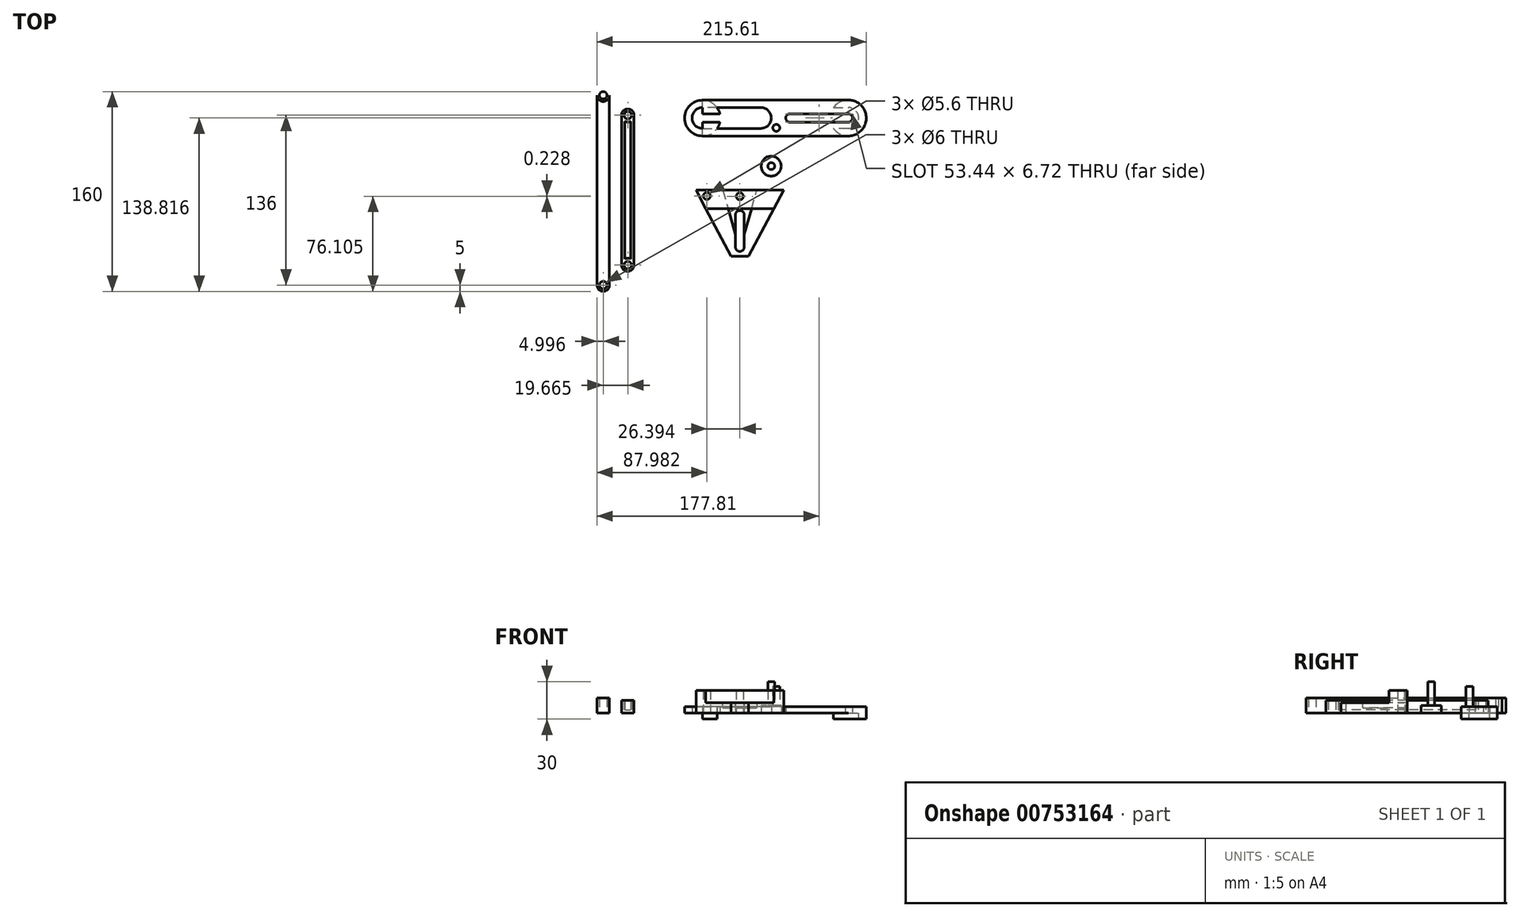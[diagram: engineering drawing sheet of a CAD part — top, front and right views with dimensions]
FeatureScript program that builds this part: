
annotation { "Feature Type Name" : "Feature", "Feature Type Description" : "" }
export const myFeature = defineFeature(function(context is Context, id is Id, definition is map)
    precondition{}
    {
        {
            var Q0;
            Q0=qCreatedBy(makeId("Top.planeOp"),FACE);
            var sketch = newSketch(context, id + "F0", { "sketchPlane" : qUnion([Q0])});
            skLineSegment(sketch, "E0.bottom", {"start": v(-59.67, 60) * mm, "end": v(-49.67, 60) * mm});
            skLineSegment(sketch, "E0.top", {"start": v(-59.67, 0) * mm, "end": v(-49.67, 0) * mm});
            skLineSegment(sketch, "E0.left", {"start": v(-59.67, 60) * mm, "end": v(-59.67, 0) * mm});
            skLineSegment(sketch, "E0.right", {"start": v(-49.67, 60) * mm, "end": v(-49.67, 0) * mm});
            skCircle(sketch, "E1", {"center": v(-54.67, 60) * mm, "radius": 5 * mm});
            skCircle(sketch, "E2.0", {"center": v(-54.67, 60) * mm, "radius": 3 * mm});
            skLineSegment(sketch, "E3.MirrorCS", {"start": v(-59.67, -60) * mm, "end": v(-49.67, -60) * mm});
            skLineSegment(sketch, "E4.MirrorCS", {"start": v(-49.67, -60) * mm, "end": v(-49.67, 0) * mm});
            skLineSegment(sketch, "E5.MirrorCS", {"start": v(-59.67, -60) * mm, "end": v(-59.67, 0) * mm});
            skCircle(sketch, "E6.MirrorC", {"center": v(-54.67, -60) * mm, "radius": 3 * mm});
            skCircle(sketch, "E7.MirrorC", {"center": v(-54.67, -60) * mm, "radius": 5 * mm});
            skSolve(sketch);
        }
        {
            var Q0;
            Q0 = qSketchRegion(id + "F0", true);
            extrude(context, id + "F1", {"entities" : qUnion([Q0]), "depth" : 10 * mm, "offsetDistance" : 25 * mm});
        }
        {
            var Q0;
            Q0=makeQuery(id+"F1.opExtrude","CAP_FACE",FACE,{"disambiguationData":[OSD([sQuery(id+"F0.wireOp",EDGE,"E0.left"),sQuery(id+"F0.wireOp",EDGE,"E0.right"),sQuery(id+"F0.wireOp",EDGE,"E1"),sQuery(id+"F0.wireOp",EDGE,"E2.0"),sQuery(id+"F0.wireOp",EDGE,"E4.MirrorCS"),sQuery(id+"F0.wireOp",EDGE,"E5.MirrorCS"),sQuery(id+"F0.wireOp",EDGE,"E6.MirrorC"),sQuery(id+"F0.wireOp",EDGE,"E7.MirrorC")])],"isStart":false});
            shell(context, id + "F2", {"entities" : qUnion([Q0]), "thickness" : 2.5 * mm});
        }
        {
            var Q0;
            Q0=qCreatedBy(makeId("Top.planeOp"),FACE);
            var sketch = newSketch(context, id + "F3", { "sketchPlane" : qUnion([Q0])});
            skLineSegment(sketch, "E8", {"start": v(70.1, 0) * mm, "end": v(42.05, -53.04) * mm});
            skLineSegment(sketch, "E9", {"start": v(42.05, -53.04) * mm, "end": v(28.05, -53.04) * mm});
            skLineSegment(sketch, "E10", {"start": v(28.05, -53.04) * mm, "end": v(0, 0) * mm});
            skLineSegment(sketch, "E11", {"start": v(0, 0) * mm, "end": v(70.1, 0) * mm});
            skCircle(sketch, "E12", {"center": v(61.44, -4.67) * mm, "radius": 2.8 * mm});
            skCircle(sketch, "E13", {"center": v(35.05, -4.9) * mm, "radius": 2.8 * mm});
            skPoint(sketch, "E13.centerSnap0", {"position": v(35.05, -53.04) * mm});
            skLineSegment(sketch, "E14", {"start": v(35.05, -53.04) * mm, "end": v(35.05, 0) * mm, "construction": true});
            skCircle(sketch, "E15.MirrorC", {"center": v(8.65, -4.67) * mm, "radius": 2.8 * mm});
            skLineSegment(sketch, "E16", {"start": v(62.33, -14.67) * mm, "end": v(7.76, -14.67) * mm});
            skCircle(sketch, "E17", {"center": v(35.05, -45.57) * mm, "radius": 3.5 * mm});
            skCircle(sketch, "E18", {"center": v(35.05, -19.75) * mm, "radius": 3.5 * mm});
            skLineSegment(sketch, "E19", {"start": v(38.55, -45.57) * mm, "end": v(38.55, -19.75) * mm});
            skLineSegment(sketch, "E20", {"start": v(31.55, -45.57) * mm, "end": v(31.55, -19.75) * mm});
            skSolve(sketch);
        }
        {
            var Q0;
            Q0 = qSketchRegion(id + "F3", true);
            extrude(context, id + "F4", {"entities" : qUnion([Q0]), "depth" : 8 * mm, "offsetDistance" : 25 * mm});
        }
        {
            var Q0;
            {var subQ2=sQuery(id+"F3.wireOp",EDGE,"E9");Q0=makeQuery(id+"F3.imprint","IMPRINT",FACE,{"disambiguationData":[TD([[makeQuery(id+"F3.imprint","IMPRINT",EDGE,{"derivedFrom":subQ2}),-1.0]])]});}
            var Q1;
            {var subQ0=sQuery(id+"F3.wireOp",EDGE,"E11");Q1=makeQuery(id+"F3.imprint","IMPRINT",FACE,{"disambiguationData":[TD([[makeQuery(id+"F3.imprint","IMPRINT",EDGE,{"derivedFrom":subQ0}),-1.0]])]});}
            extrude(context, id + "F5", {"entities" : qUnion([Q0, Q1]), "depth" : 8 * mm, "offsetDistance" : 25 * mm});
        }
        {
            var Q0;
            Q0=makeQuery(id+"F4.opExtrude","CAP_FACE",FACE,{"disambiguationData":[OSD([sQuery(id+"F3.wireOp",EDGE,"E8"),sQuery(id+"F3.wireOp",EDGE,"E9"),sQuery(id+"F3.wireOp",EDGE,"E10"),sQuery(id+"F3.wireOp",EDGE,"E16")])],"isStart":false});
            shell(context, id + "F6", {"entities" : qUnion([Q0]), "thickness" : 2.5 * mm});
        }
        {
            var Q0;
            Q0=makeQuery(id+"F3.imprint","IMPRINT",FACE,{"disambiguationData":[TD([[makeQuery(id+"F3.imprint","IMPRINT",EDGE,{"derivedFrom":sQuery(id+"F3.wireOp",EDGE,"E12")}),1.0]])]});
            var Q1;
            Q1=makeQuery(id+"F3.imprint","IMPRINT",FACE,{"disambiguationData":[TD([[makeQuery(id+"F3.imprint","IMPRINT",EDGE,{"derivedFrom":sQuery(id+"F3.wireOp",EDGE,"E15.MirrorC")}),-1.0]])]});
            extrude(context, id + "F7", {"entities" : qUnion([Q0, Q1]), "operationType" : NewBodyOperationType.ADD, "depth" : 18 * mm, "offsetDistance" : 25 * mm});
        }
        {
            var Q0;
            Q0=qCreatedBy(makeId("Top.planeOp"),FACE);
            var sketch = newSketch(context, id + "F8", { "sketchPlane" : qUnion([Q0])});
            skLineSegment(sketch, "E21.bottom", {"start": v(121.84, 43.38) * mm, "end": v(5.16, 43.38) * mm});
            skLineSegment(sketch, "E21.top", {"start": v(121.84, 72.06) * mm, "end": v(5.16, 72.06) * mm});
            skLineSegment(sketch, "E21.left", {"start": v(121.84, 43.38) * mm, "end": v(121.84, 54.45) * mm});
            skLineSegment(sketch, "E21.right", {"start": v(5.16, 43.38) * mm, "end": v(5.16, 72.06) * mm});
            skCircle(sketch, "E22", {"center": v(121.84, 57.82) * mm, "radius": 14.44 * mm});
            skCircle(sketch, "E23", {"center": v(5.16, 57.72) * mm, "radius": 14.34 * mm});
            skArc(sketch, "E24", {"start": v(121.84, 54.45) * mm, "mid": v(125.2, 57.82) * mm, "end": v(121.84, 61.18) * mm});
            skLineSegment(sketch, "E25", {"start": v(63.5, 43.38) * mm, "end": v(63.5, 72.06) * mm, "construction": true});
            skArc(sketch, "E26", {"start": v(75.12, 61.18) * mm, "mid": v(71.76, 57.82) * mm, "end": v(75.12, 54.45) * mm});
            skLineSegment(sketch, "E27", {"start": v(121.84, 54.45) * mm, "end": v(75.12, 54.45) * mm});
            skLineSegment(sketch, "E28", {"start": v(75.12, 61.18) * mm, "end": v(121.84, 61.18) * mm});
            skCircle(sketch, "E29.MirrorC", {"center": v(51.88, 57.82) * mm, "radius": 3.36 * mm});
            skLineSegment(sketch, "E30.MirrorCS", {"start": v(5.16, 54.45) * mm, "end": v(51.88, 54.45) * mm});
            skLineSegment(sketch, "E31.MirrorCS", {"start": v(51.88, 61.18) * mm, "end": v(5.16, 61.18) * mm});
            skCircle(sketch, "E32.MirrorC", {"center": v(5.16, 57.82) * mm, "radius": 3.36 * mm});
            skLineSegment(sketch, "E33.trimOffspring", {"start": v(121.84, 61.18) * mm, "end": v(121.84, 72.06) * mm});
            skLineSegment(sketch, "E34.0", {"start": v(75.12, 66.18) * mm, "end": v(121.84, 66.18) * mm});
            skArc(sketch, "E34.1", {"start": v(75.12, 66.18) * mm, "mid": v(66.76, 57.82) * mm, "end": v(75.12, 49.45) * mm});
            skLineSegment(sketch, "E34.2", {"start": v(121.84, 49.45) * mm, "end": v(75.12, 49.45) * mm});
            skArc(sketch, "E34.3", {"start": v(121.84, 49.45) * mm, "mid": v(130.2, 57.82) * mm, "end": v(121.84, 66.18) * mm});
            skArc(sketch, "E35.MirrorCS", {"start": v(51.88, 66.18) * mm, "mid": v(60.24, 57.82) * mm, "end": v(51.88, 49.45) * mm});
            skLineSegment(sketch, "E36.MirrorCS", {"start": v(51.88, 66.18) * mm, "end": v(5.16, 66.18) * mm});
            skLineSegment(sketch, "E37.MirrorCS", {"start": v(5.16, 49.45) * mm, "end": v(51.88, 49.45) * mm});
            skArc(sketch, "E38.MirrorCS", {"start": v(5.16, 49.45) * mm, "mid": v(-3.2, 57.82) * mm, "end": v(5.16, 66.18) * mm});
            skSolve(sketch);
        }
        {
            var Q0;
            Q0 = qSketchRegion(id + "F8", true);
            var Q1;
            {var subQ0=sQuery(id+"F8.wireOp",EDGE,"E34.0");var subQ1=sQuery(id+"F8.wireOp",EDGE,"E22");var subQ2=makeQuery(id+"F8.imprint","INTERSECT",VERTEX,{"derivedFrom":[subQ1,subQ0]});Q1=makeQuery(id+"F8.imprint","IMPRINT",FACE,{"disambiguationData":[TD([[makeQuery(id+"F8.imprint","IMPRINT",EDGE,{"disambiguationData":[TD([[subQ2,-1.0]])],"derivedFrom":subQ1}),1.0]])]});}
            var Q2;
            {var subQ0=sQuery(id+"F8.wireOp",EDGE,"E24");Q2=makeQuery(id+"F8.imprint","IMPRINT",FACE,{"disambiguationData":[TD([[makeQuery(id+"F8.imprint","IMPRINT",EDGE,{"derivedFrom":subQ0}),-1.0]])]});}
            var Q3;
            {var subQ1=sQuery(id+"F8.wireOp",EDGE,"E26");Q3=makeQuery(id+"F8.imprint","IMPRINT",FACE,{"disambiguationData":[TD([[makeQuery(id+"F8.imprint","IMPRINT",EDGE,{"derivedFrom":subQ1}),-1.0]])]});}
            var Q4;
            {var subQ0=sQuery(id+"F8.wireOp",EDGE,"E27");var subQ5=sQuery(id+"F8.wireOp",EDGE,"E22");var subQ6=makeQuery(id+"F8.imprint","INTERSECT",VERTEX,{"derivedFrom":[subQ5,subQ0]});Q4=makeQuery(id+"F8.imprint","IMPRINT",FACE,{"disambiguationData":[TD([[makeQuery(id+"F8.imprint","IMPRINT",EDGE,{"disambiguationData":[TD([[subQ6,-1.0]])],"derivedFrom":subQ5}),1.0]])]});}
            var Q5;
            {var subQ12=sQuery(id+"F8.wireOp",EDGE,"E35.MirrorCS");Q5=makeQuery(id+"F8.imprint","IMPRINT",FACE,{"disambiguationData":[TD([[makeQuery(id+"F8.imprint","IMPRINT",EDGE,{"derivedFrom":subQ12}),-1.0]])]});}
            var Q6;
            {var subQ3=sQuery(id+"F8.wireOp",EDGE,"E37.MirrorCS");var subQ5=sQuery(id+"F8.wireOp",EDGE,"E23");var subQ6=makeQuery(id+"F8.imprint","INTERSECT",VERTEX,{"derivedFrom":[subQ5,subQ3]});Q6=makeQuery(id+"F8.imprint","IMPRINT",FACE,{"disambiguationData":[TD([[makeQuery(id+"F8.imprint","IMPRINT",EDGE,{"disambiguationData":[TD([[subQ6,-1.0]])],"derivedFrom":subQ5}),1.0]])]});}
            var Q7;
            {var subQ3=sQuery(id+"F8.wireOp",EDGE,"E36.MirrorCS");var subQ5=sQuery(id+"F8.wireOp",EDGE,"E23");var subQ7=makeQuery(id+"F8.imprint","INTERSECT",VERTEX,{"derivedFrom":[subQ5,subQ3]});Q7=makeQuery(id+"F8.imprint","IMPRINT",FACE,{"disambiguationData":[TD([[makeQuery(id+"F8.imprint","IMPRINT",EDGE,{"disambiguationData":[TD([[subQ7,1.0]])],"derivedFrom":subQ5}),1.0]])]});}
            var Q8;
            {var subQ3=sQuery(id+"F8.wireOp",EDGE,"E38.MirrorCS");Q8=makeQuery(id+"F8.imprint","IMPRINT",FACE,{"disambiguationData":[TD([[makeQuery(id+"F8.imprint","IMPRINT",EDGE,{"derivedFrom":subQ3}),-1.0]])]});}
            extrude(context, id + "F9", {"entities" : qUnion([Q0, Q1, Q2, Q3, Q4, Q5, Q6, Q7, Q8]), "endBound" : BoundingType.SYMMETRIC, "depth" : 10 * mm, "offsetDistance" : 25 * mm});
        }
        {
            var Q0;
            Q0=qCreatedBy(makeId("Top.planeOp"),FACE);
            var sketch = newSketch(context, id + "F10", { "sketchPlane" : qUnion([Q0])});
            skCircle(sketch, "E39", {"center": v(60.19, 19.28) * mm, "radius": 8 * mm});
            skCircle(sketch, "E40", {"center": v(60.19, 19.28) * mm, "radius": 2.8 * mm});
            skSolve(sketch);
        }
        {
            var Q0;
            Q0 = qSketchRegion(id + "F10", true);
            var Q1;
            Q1=makeQuery(id+"F10.imprint","IMPRINT",FACE,{"disambiguationData":[TD([[makeQuery(id+"F10.imprint","IMPRINT",EDGE,{"derivedFrom":sQuery(id+"F10.wireOp",EDGE,"E40")}),1.0]])]});
            extrude(context, id + "F11", {"entities" : qUnion([Q0, Q1]), "depth" : 6 * mm, "offsetDistance" : 25 * mm});
        }
        {
            var Q0;
            Q0=makeQuery(id+"F10.imprint","IMPRINT",FACE,{"disambiguationData":[TD([[makeQuery(id+"F10.imprint","IMPRINT",EDGE,{"derivedFrom":sQuery(id+"F10.wireOp",EDGE,"E40")}),1.0]])]});
            extrude(context, id + "F12", {"entities" : qUnion([Q0]), "operationType" : NewBodyOperationType.ADD, "depth" : 25 * mm, "offsetDistance" : 25 * mm});
        }
        {
            var Q0;
            {var subQ0=sQuery(id+"F8.wireOp",EDGE,"E27");var subQ5=sQuery(id+"F8.wireOp",EDGE,"E22");var subQ6=makeQuery(id+"F8.imprint","INTERSECT",VERTEX,{"derivedFrom":[subQ5,subQ0]});Q0=makeQuery(id+"F8.imprint","IMPRINT",FACE,{"disambiguationData":[TD([[makeQuery(id+"F8.imprint","IMPRINT",EDGE,{"disambiguationData":[TD([[subQ6,-1.0]])],"derivedFrom":subQ5}),1.0]])]});}
            var Q1;
            {var subQ0=sQuery(id+"F8.wireOp",EDGE,"E24");Q1=makeQuery(id+"F8.imprint","IMPRINT",FACE,{"disambiguationData":[TD([[makeQuery(id+"F8.imprint","IMPRINT",EDGE,{"derivedFrom":subQ0}),-1.0]])]});}
            var Q2;
            {var subQ0=sQuery(id+"F8.wireOp",EDGE,"E34.0");var subQ1=sQuery(id+"F8.wireOp",EDGE,"E22");var subQ2=makeQuery(id+"F8.imprint","INTERSECT",VERTEX,{"derivedFrom":[subQ1,subQ0]});Q2=makeQuery(id+"F8.imprint","IMPRINT",FACE,{"disambiguationData":[TD([[makeQuery(id+"F8.imprint","IMPRINT",EDGE,{"disambiguationData":[TD([[subQ2,-1.0]])],"derivedFrom":subQ1}),1.0]])]});}
            var Q3;
            {var subQ1=sQuery(id+"F8.wireOp",EDGE,"E26");Q3=makeQuery(id+"F8.imprint","IMPRINT",FACE,{"disambiguationData":[TD([[makeQuery(id+"F8.imprint","IMPRINT",EDGE,{"derivedFrom":subQ1}),-1.0]])]});}
            var Q4;
            {var subQ12=sQuery(id+"F8.wireOp",EDGE,"E35.MirrorCS");Q4=makeQuery(id+"F8.imprint","IMPRINT",FACE,{"disambiguationData":[TD([[makeQuery(id+"F8.imprint","IMPRINT",EDGE,{"derivedFrom":subQ12}),-1.0]])]});}
            var Q5;
            {var subQ3=sQuery(id+"F8.wireOp",EDGE,"E37.MirrorCS");var subQ5=sQuery(id+"F8.wireOp",EDGE,"E23");var subQ6=makeQuery(id+"F8.imprint","INTERSECT",VERTEX,{"derivedFrom":[subQ5,subQ3]});Q5=makeQuery(id+"F8.imprint","IMPRINT",FACE,{"disambiguationData":[TD([[makeQuery(id+"F8.imprint","IMPRINT",EDGE,{"disambiguationData":[TD([[subQ6,-1.0]])],"derivedFrom":subQ5}),1.0]])]});}
            var Q6;
            {var subQ3=sQuery(id+"F8.wireOp",EDGE,"E38.MirrorCS");Q6=makeQuery(id+"F8.imprint","IMPRINT",FACE,{"disambiguationData":[TD([[makeQuery(id+"F8.imprint","IMPRINT",EDGE,{"derivedFrom":subQ3}),-1.0]])]});}
            var Q7;
            {var subQ3=sQuery(id+"F8.wireOp",EDGE,"E36.MirrorCS");var subQ5=sQuery(id+"F8.wireOp",EDGE,"E23");var subQ7=makeQuery(id+"F8.imprint","INTERSECT",VERTEX,{"derivedFrom":[subQ5,subQ3]});Q7=makeQuery(id+"F8.imprint","IMPRINT",FACE,{"disambiguationData":[TD([[makeQuery(id+"F8.imprint","IMPRINT",EDGE,{"disambiguationData":[TD([[subQ7,1.0]])],"derivedFrom":subQ5}),1.0]])]});}
            extrude(context, id + "F13", {"entities" : qUnion([Q0, Q1, Q2, Q3, Q4, Q5, Q6, Q7]), "operationType" : NewBodyOperationType.REMOVE, "oppositeDirection" : true, "depth" : 25 * mm, "offsetDistance" : 25 * mm});
        }
        {
            var Q0;
            Q0=makeQuery(id+"F9.opExtrude","CAP_FACE",FACE,{"disambiguationData":[OSD([sQuery(id+"F8.wireOp",EDGE,"E21.bottom"),sQuery(id+"F8.wireOp",EDGE,"E21.top"),sQuery(id+"F8.wireOp",EDGE,"E22"),sQuery(id+"F8.wireOp",EDGE,"E23"),sQuery(id+"F8.wireOp",EDGE,"E24"),sQuery(id+"F8.wireOp",EDGE,"E26"),sQuery(id+"F8.wireOp",EDGE,"E27"),sQuery(id+"F8.wireOp",EDGE,"E28"),sQuery(id+"F8.wireOp",EDGE,"E29.MirrorC"),sQuery(id+"F8.wireOp",EDGE,"E30.MirrorCS"),sQuery(id+"F8.wireOp",EDGE,"E31.MirrorCS"),sQuery(id+"F8.wireOp",EDGE,"E32.MirrorC")])],"isStart":false});
            var sketch = newSketch(context, id + "F14", { "sketchPlane" : qUnion([Q0])});
            skCircle(sketch, "E41", {"center": v(64.28, 49.92) * mm, "radius": 2.8 * mm});
            skSolve(sketch);
        }
        {
            var Q0;
            Q0 = qSketchRegion(id + "F14", true);
            extrude(context, id + "F15", {"entities" : qUnion([Q0]), "operationType" : NewBodyOperationType.ADD, "depth" : 16 * mm, "offsetDistance" : 25 * mm});
        }
        {
            var Q0;
            Q0=qCreatedBy(makeId("Top.planeOp"),FACE);
            var sketch = newSketch(context, id + "F16", { "sketchPlane" : qUnion([Q0])});
            skLineSegment(sketch, "E42.bottom", {"start": v(-69.33, -76) * mm, "end": v(-79.33, -76) * mm});
            skLineSegment(sketch, "E42.top", {"start": v(-69.33, 0) * mm, "end": v(-79.33, 0) * mm});
            skLineSegment(sketch, "E42.left", {"start": v(-69.33, -76) * mm, "end": v(-69.33, 0) * mm});
            skLineSegment(sketch, "E42.right", {"start": v(-79.33, -76) * mm, "end": v(-79.33, 0) * mm});
            skCircle(sketch, "E43", {"center": v(-74.33, -76) * mm, "radius": 5 * mm});
            skCircle(sketch, "E44", {"center": v(-74.33, -76) * mm, "radius": 3 * mm});
            skLineSegment(sketch, "E45.MirrorCS", {"start": v(-69.33, 76) * mm, "end": v(-79.33, 76) * mm});
            skCircle(sketch, "E46.MirrorC", {"center": v(-74.33, 76) * mm, "radius": 5 * mm});
            skLineSegment(sketch, "E47.MirrorCS", {"start": v(-69.33, 76) * mm, "end": v(-69.33, 0) * mm});
            skLineSegment(sketch, "E48.MirrorCS", {"start": v(-79.33, 76) * mm, "end": v(-79.33, 0) * mm});
            skCircle(sketch, "E49.MirrorC", {"center": v(-74.33, 76) * mm, "radius": 3 * mm});
            skSolve(sketch);
        }
        {
            var Q0;
            Q0=makeQuery(id+"F16.imprint","IMPRINT",FACE,{"disambiguationData":[TD([[makeQuery(id+"F16.imprint","IMPRINT",EDGE,{"derivedFrom":sQuery(id+"F16.wireOp",EDGE,"E42.top")}),1.0]])]});
            var Q1;
            {var subQ1=sQuery(id+"F16.wireOp",EDGE,"E42.bottom");var subQ3=sQuery(id+"F16.wireOp",EDGE,"E44");var subQ4=makeQuery(id+"F16.imprint","INTERSECT",VERTEX,{"disambiguationData":[OD(0.0)],"derivedFrom":[subQ1,subQ3]});Q1=makeQuery(id+"F16.imprint","IMPRINT",FACE,{"disambiguationData":[TD([[makeQuery(id+"F16.imprint","IMPRINT",EDGE,{"disambiguationData":[TD([[subQ4,-1.0]])],"derivedFrom":subQ3}),-1.0]])]});}
            var Q2;
            {var subQ1=sQuery(id+"F16.wireOp",EDGE,"E45.MirrorCS");var subQ3=sQuery(id+"F16.wireOp",EDGE,"E49.MirrorC");var subQ4=makeQuery(id+"F16.imprint","INTERSECT",VERTEX,{"disambiguationData":[OD(0.0)],"derivedFrom":[subQ1,subQ3]});Q2=makeQuery(id+"F16.imprint","IMPRINT",FACE,{"disambiguationData":[TD([[makeQuery(id+"F16.imprint","IMPRINT",EDGE,{"disambiguationData":[TD([[subQ4,1.0]])],"derivedFrom":subQ3}),1.0]])]});}
            var Q3;
            Q3=makeQuery(id+"F16.imprint","IMPRINT",FACE,{"disambiguationData":[TD([[makeQuery(id+"F16.imprint","IMPRINT",EDGE,{"derivedFrom":sQuery(id+"F16.wireOp",EDGE,"E42.top")}),-1.0]])]});
            var Q4;
            {var subQ1=sQuery(id+"F16.wireOp",EDGE,"E45.MirrorCS");var subQ3=sQuery(id+"F16.wireOp",EDGE,"E49.MirrorC");var subQ4=makeQuery(id+"F16.imprint","INTERSECT",VERTEX,{"disambiguationData":[OD(0.0)],"derivedFrom":[subQ1,subQ3]});Q4=makeQuery(id+"F16.imprint","IMPRINT",FACE,{"disambiguationData":[TD([[makeQuery(id+"F16.imprint","IMPRINT",EDGE,{"disambiguationData":[TD([[subQ4,-1.0]])],"derivedFrom":subQ3}),1.0]])]});}
            var Q5;
            {var subQ1=sQuery(id+"F16.wireOp",EDGE,"E42.bottom");var subQ3=sQuery(id+"F16.wireOp",EDGE,"E44");var subQ4=makeQuery(id+"F16.imprint","INTERSECT",VERTEX,{"disambiguationData":[OD(0.0)],"derivedFrom":[subQ1,subQ3]});Q5=makeQuery(id+"F16.imprint","IMPRINT",FACE,{"disambiguationData":[TD([[makeQuery(id+"F16.imprint","IMPRINT",EDGE,{"disambiguationData":[TD([[subQ4,1.0]])],"derivedFrom":subQ3}),-1.0]])]});}
            extrude(context, id + "F17", {"entities" : qUnion([Q0, Q1, Q2, Q3, Q4, Q5]), "depth" : 12 * mm, "offsetDistance" : 25 * mm});
        }
        {
            var Q0;
            Q0=makeQuery(id+"F5.opExtrude","CAP_FACE",FACE,{"disambiguationData":[OSD([sQuery(id+"F3.wireOp",EDGE,"E8"),sQuery(id+"F3.wireOp",EDGE,"E9"),sQuery(id+"F3.wireOp",EDGE,"E10"),sQuery(id+"F3.wireOp",EDGE,"E11"),sQuery(id+"F3.wireOp",EDGE,"E12"),sQuery(id+"F3.wireOp",EDGE,"E13"),sQuery(id+"F3.wireOp",EDGE,"E15.MirrorC"),sQuery(id+"F3.wireOp",EDGE,"E17"),sQuery(id+"F3.wireOp",EDGE,"E18"),sQuery(id+"F3.wireOp",EDGE,"E19"),sQuery(id+"F3.wireOp",EDGE,"E20")])],"isStart":false});
            var sketch = newSketch(context, id + "F18", { "sketchPlane" : qUnion([Q0])});
            skLineSegment(sketch, "E50", {"start": v(50.44, 6.51) * mm, "end": v(19.65, 6.51) * mm});
            skLineSegment(sketch, "E51", {"start": v(19.65, 6.51) * mm, "end": v(31.55, -35.4) * mm});
            skLineSegment(sketch, "E52", {"start": v(31.55, -35.4) * mm, "end": v(38.55, -35.4) * mm});
            skLineSegment(sketch, "E53", {"start": v(38.55, -35.4) * mm, "end": v(50.44, 6.51) * mm});
            skSolve(sketch);
        }
        {
            var Q0;
            Q0 = qSketchRegion(id + "F18", true);
            extrude(context, id + "F19", {"entities" : qUnion([Q0]), "operationType" : NewBodyOperationType.REMOVE, "oppositeDirection" : true, "depth" : 4 * mm, "offsetDistance" : 25 * mm});
        }
    });
